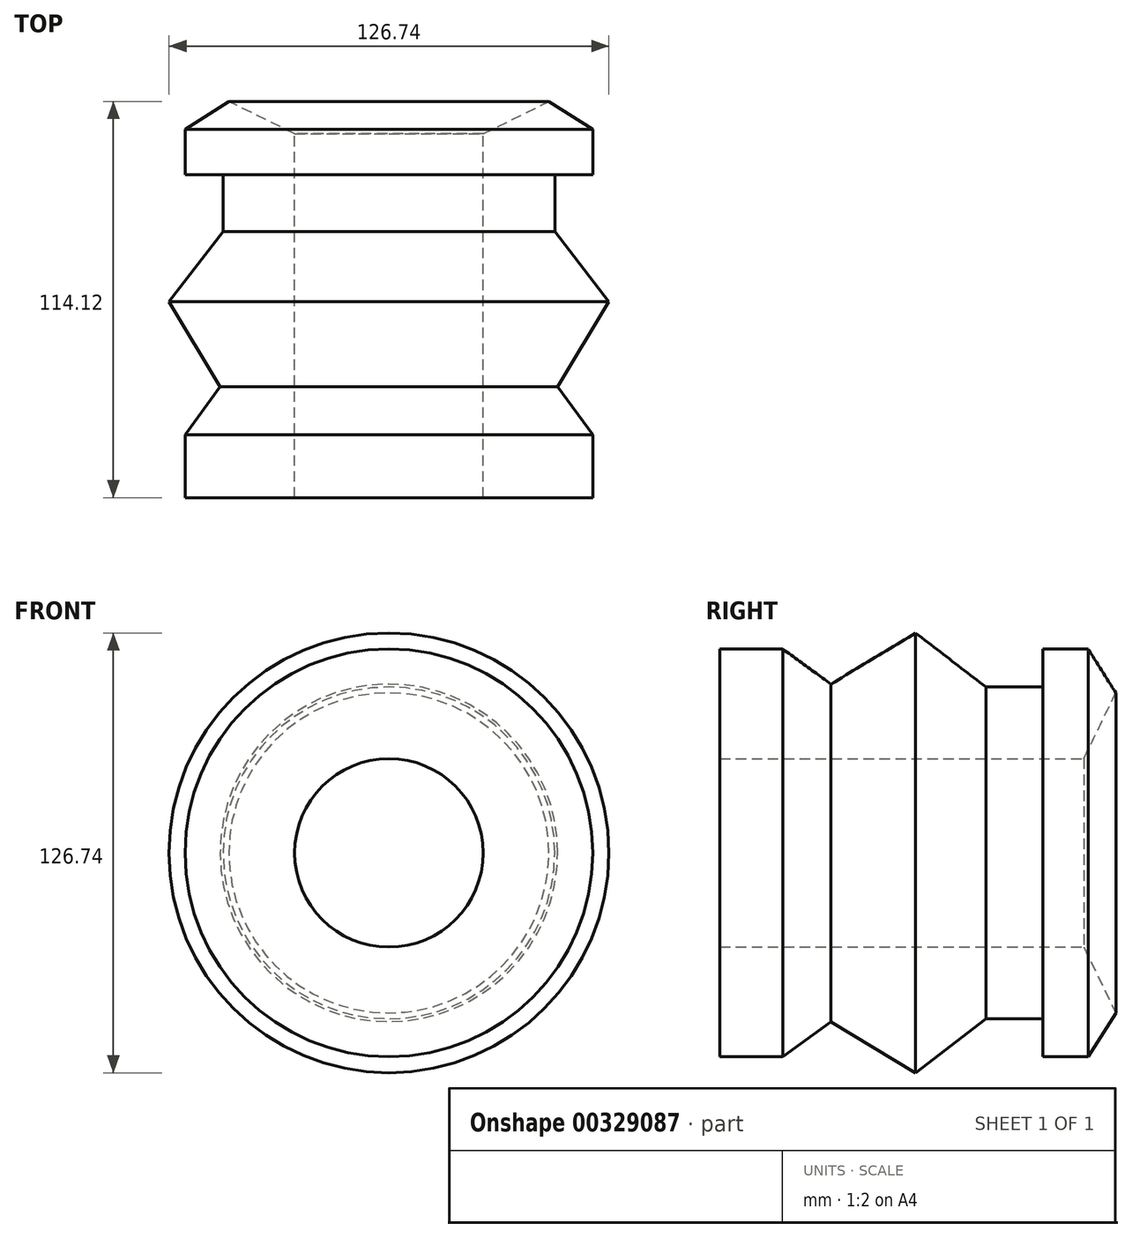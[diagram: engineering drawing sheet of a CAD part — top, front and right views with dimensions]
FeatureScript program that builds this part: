
annotation { "Feature Type Name" : "Feature", "Feature Type Description" : "" }
export const myFeature = defineFeature(function(context is Context, id is Id, definition is map)
    precondition{}
    {
        {
            var Q0;
            Q0=qCreatedBy(makeId("Top.planeOp"),FACE);
            var sketch = newSketch(context, id + "F0", { "sketchPlane" : qUnion([Q0])});
            skLineSegment(sketch, "E0", {"start": v(-27.16, 54.74) * mm, "end": v(-27.16, -50.1) * mm});
            skLineSegment(sketch, "E1", {"start": v(-27.16, -50.1) * mm, "end": v(-58.74, -50.1) * mm});
            skLineSegment(sketch, "E2", {"start": v(-58.74, -50.1) * mm, "end": v(-58.74, -32) * mm});
            skLineSegment(sketch, "E3", {"start": v(-58.74, -32) * mm, "end": v(-48.64, -18.1) * mm});
            skLineSegment(sketch, "E4", {"start": v(-48.64, -18.1) * mm, "end": v(-63.37, 6.32) * mm});
            skLineSegment(sketch, "E5", {"start": v(-63.37, 6.32) * mm, "end": v(-47.8, 26.53) * mm});
            skLineSegment(sketch, "E6", {"start": v(-47.8, 26.53) * mm, "end": v(-47.8, 42.95) * mm});
            skLineSegment(sketch, "E7", {"start": v(-47.8, 42.95) * mm, "end": v(-58.74, 42.95) * mm});
            skLineSegment(sketch, "E8", {"start": v(-58.74, 42.95) * mm, "end": v(-58.74, 56) * mm});
            skLineSegment(sketch, "E9", {"start": v(-58.74, 56) * mm, "end": v(-46.1, 64) * mm});
            skLineSegment(sketch, "E10", {"start": v(-46.1, 64) * mm, "end": v(-27.16, 54.74) * mm});
            skLineSegment(sketch, "E11", {"start": v(0, 61.48) * mm, "end": v(0, -51.8) * mm, "construction": true});
            skSolve(sketch);
        }
        {
            var Q0;
            Q0=makeQuery(id+"F0.imprint","IMPRINT",FACE,{"disambiguationData":[TD([[makeQuery(id+"F0.imprint","IMPRINT",EDGE,{"derivedFrom":sQuery(id+"F0.wireOp",EDGE,"E0")}),-1.0]])]});
            var Q1;
            Q1=sQuery(id+"F0.wireOp",EDGE,"E11");
            revolve(context, id + "F1", {"surfaceOperationType" : NewSurfaceOperationType.NEW, "entities" : qUnion([Q0]), "axis" : qUnion([Q1]), "revolveType" : RevolveType.FULL});
        }
    });
